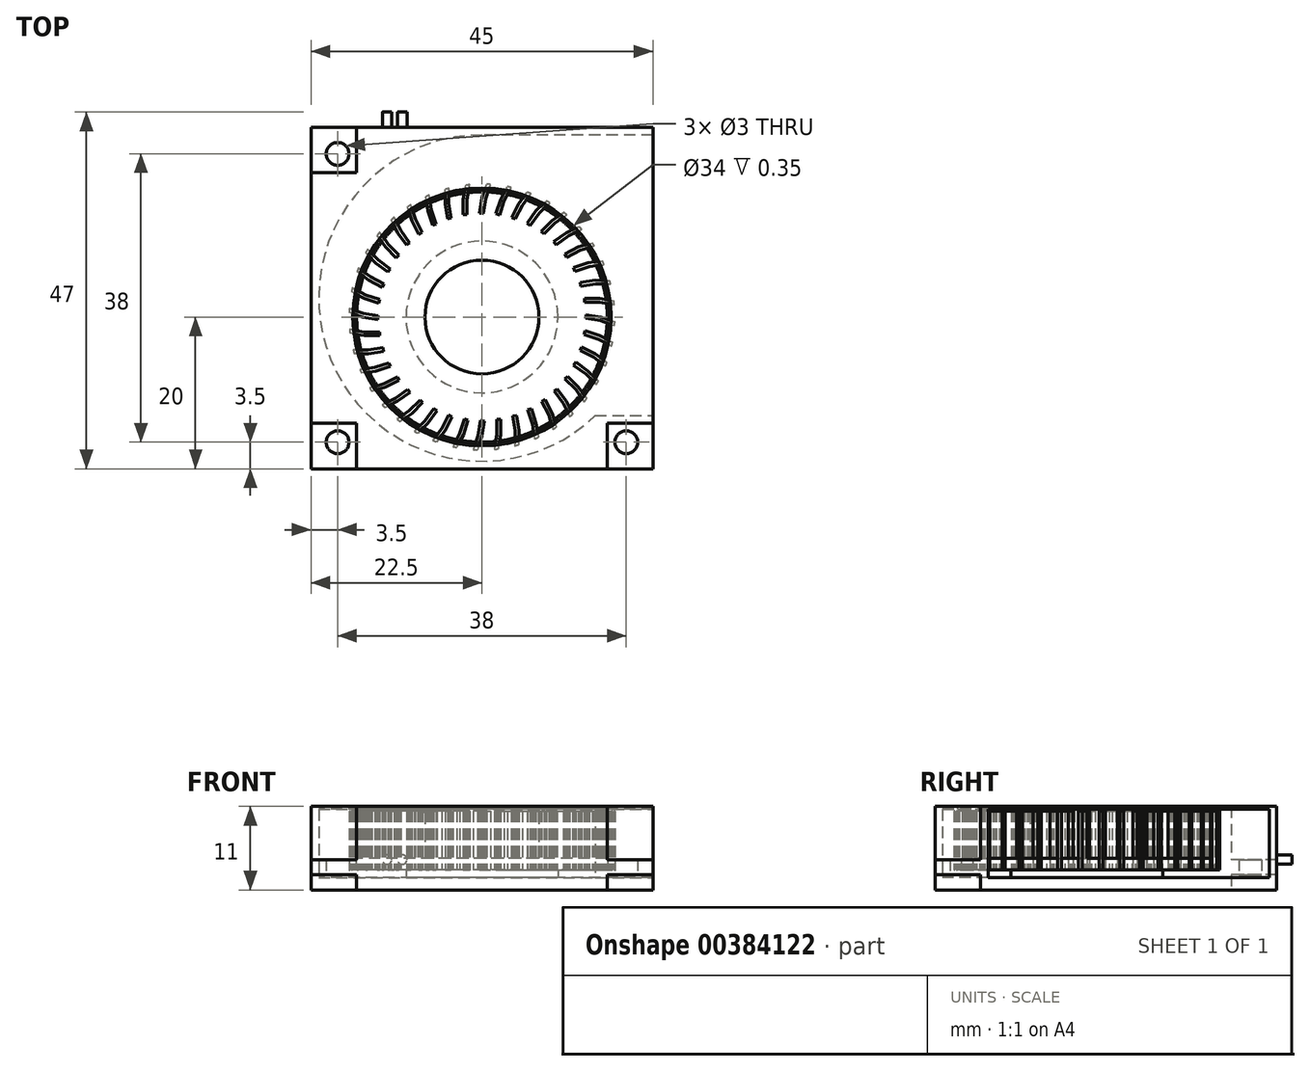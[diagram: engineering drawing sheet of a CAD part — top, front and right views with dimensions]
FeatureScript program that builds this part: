
annotation { "Feature Type Name" : "Feature", "Feature Type Description" : "" }
export const myFeature = defineFeature(function(context is Context, id is Id, definition is map)
    precondition{}
    {
        {
            var Q0;
            Q0=qCreatedBy(makeId("Top.planeOp"),FACE);
            var sketch = newSketch(context, id + "F0", { "sketchPlane" : qUnion([Q0])});
            skLineSegment(sketch, "E0", {"start": v(0, 27.21) * mm, "end": v(0, -23.79) * mm, "construction": true});
            skLineSegment(sketch, "E1", {"start": v(-25.54, 0) * mm, "end": v(25.6, 0) * mm, "construction": true});
            skLineSegment(sketch, "E2.bottom", {"start": v(-16.5, 25) * mm, "end": v(22.5, 25) * mm});
            skLineSegment(sketch, "E2.top", {"start": v(-16.5, -20) * mm, "end": v(16.5, -20) * mm});
            skLineSegment(sketch, "E2.left", {"start": v(-22.5, 19) * mm, "end": v(-22.5, -14) * mm});
            skLineSegment(sketch, "E2.right", {"start": v(22.5, 25) * mm, "end": v(22.5, -14) * mm});
            skLineSegment(sketch, "E3", {"start": v(-22.5, 19) * mm, "end": v(-16.5, 19) * mm});
            skLineSegment(sketch, "E4", {"start": v(-16.5, 19) * mm, "end": v(-16.5, 25) * mm});
            skLineSegment(sketch, "E5", {"start": v(-16.5, -14) * mm, "end": v(-16.5, -20) * mm});
            skLineSegment(sketch, "E6", {"start": v(-16.5, -14) * mm, "end": v(-22.5, -14) * mm});
            skLineSegment(sketch, "E7", {"start": v(16.5, -14) * mm, "end": v(16.5, -20) * mm});
            skLineSegment(sketch, "E8", {"start": v(16.5, -14) * mm, "end": v(22.5, -14) * mm});
            skLineSegment(sketch, "E9", {"start": v(-25.95, 2.5) * mm, "end": v(25.4, 2.5) * mm, "construction": true});
            skSolve(sketch);
        }
        {
            var Q0;
            Q0=qSketchRegion(id+"F0",true);
            extrude(context, id + "F1", {"entities" : qUnion([Q0]), "depth" : 11 * mm, "offsetDistance" : 25 * mm});
        }
        {
            var Q0;
            Q0=qCreatedBy(makeId("Top.planeOp"),FACE);
            cPlane(context, id + "F2", {"entities" : qUnion([Q0]), "cplaneType" : CPlaneType.OFFSET, "offset" : 2 * mm, "width" : 150 * mm, "height" : 150 * mm});
        }
        {
            var Q0;
            Q0=qCreatedBy(id+"F2.planeOp",FACE);
            var sketch = newSketch(context, id + "F3", { "sketchPlane" : qUnion([Q0])});
            skCircle(sketch, "E10", {"center": v(-19, 21.5) * mm, "radius": 1.5 * mm});
            skCircle(sketch, "E11", {"center": v(-19, -16.5) * mm, "radius": 1.5 * mm});
            skCircle(sketch, "E12", {"center": v(19, -16.5) * mm, "radius": 1.5 * mm});
            skLineSegment(sketch, "E13", {"start": v(-26.25, 2.5) * mm, "end": v(24.75, 2.5) * mm, "construction": true});
            skLineSegment(sketch, "E14.bottom", {"start": v(-22.5, 25) * mm, "end": v(-16.5, 25) * mm});
            skLineSegment(sketch, "E14.top", {"start": v(-22.5, 19) * mm, "end": v(-16.5, 19) * mm});
            skLineSegment(sketch, "E14.left", {"start": v(-16.5, 25) * mm, "end": v(-16.5, 19) * mm});
            skLineSegment(sketch, "E14.right", {"start": v(-22.5, 25) * mm, "end": v(-22.5, 19) * mm});
            skLineSegment(sketch, "E15.bottom", {"start": v(-22.5, -14) * mm, "end": v(-16.5, -14) * mm});
            skLineSegment(sketch, "E15.top", {"start": v(-22.5, -20) * mm, "end": v(-16.5, -20) * mm});
            skLineSegment(sketch, "E15.left", {"start": v(-16.5, -14) * mm, "end": v(-16.5, -20) * mm});
            skLineSegment(sketch, "E15.right", {"start": v(-22.5, -14) * mm, "end": v(-22.5, -20) * mm});
            skLineSegment(sketch, "E16.bottom", {"start": v(16.5, -14) * mm, "end": v(22.5, -14) * mm});
            skLineSegment(sketch, "E16.top", {"start": v(16.5, -20) * mm, "end": v(22.5, -20) * mm});
            skLineSegment(sketch, "E16.left", {"start": v(22.5, -14) * mm, "end": v(22.5, -20) * mm});
            skLineSegment(sketch, "E16.right", {"start": v(16.5, -14) * mm, "end": v(16.5, -20) * mm});
            skSolve(sketch);
        }
        {
            var Q0;
            Q0=qSketchRegion(id+"F3",true);
            extrude(context, id + "F4", {"entities" : qUnion([Q0]), "operationType" : NewBodyOperationType.ADD, "depth" : 2 * mm, "offsetDistance" : 25 * mm});
        }
        {
            var Q0;
            Q0=qCreatedBy(makeId("Top.planeOp"),FACE);
            cPlane(context, id + "F5", {"entities" : qUnion([Q0]), "cplaneType" : CPlaneType.OFFSET, "offset" : 1.65 * mm, "width" : 150 * mm, "height" : 150 * mm});
        }
        {
            var Q0;
            Q0=qCreatedBy(id+"F5.planeOp",FACE);
            var sketch = newSketch(context, id + "F6", { "sketchPlane" : qUnion([Q0])});
            skLineSegment(sketch, "E17", {"start": v(22.5, 24) * mm, "end": v(0, 24) * mm});
            skArc(sketch, "E18", {"start": v(0, 24) * mm, "mid": v(-19.94, -5.53) * mm, "end": v(14.9, -13) * mm});
            skLineSegment(sketch, "E19", {"start": v(14.9, -13) * mm, "end": v(22.5, -13) * mm});
            skLineSegment(sketch, "E20", {"start": v(22.5, -13) * mm, "end": v(22.5, 24) * mm});
            skSolve(sketch);
        }
        {
            var Q0;
            Q0=qSketchRegion(id+"F6",true);
            extrude(context, id + "F7", {"entities" : qUnion([Q0]), "operationType" : NewBodyOperationType.REMOVE, "depth" : 9 * mm, "offsetDistance" : 25 * mm});
        }
        {
            var Q0;
            Q0=makeQuery(id+"F1.opExtrude","CAP_FACE",FACE,{"disambiguationData":[OSD([sQuery(id+"F0.wireOp",EDGE,"E2.bottom"),sQuery(id+"F0.wireOp",EDGE,"E2.top"),sQuery(id+"F0.wireOp",EDGE,"E2.left"),sQuery(id+"F0.wireOp",EDGE,"E2.right"),sQuery(id+"F0.wireOp",EDGE,"E3"),sQuery(id+"F0.wireOp",EDGE,"E4"),sQuery(id+"F0.wireOp",EDGE,"E5"),sQuery(id+"F0.wireOp",EDGE,"E6"),sQuery(id+"F0.wireOp",EDGE,"E7"),sQuery(id+"F0.wireOp",EDGE,"E8")])],"isStart":false});
            var sketch = newSketch(context, id + "F8", { "sketchPlane" : qUnion([Q0])});
            skCircle(sketch, "E21", {"center": v(0, 0) * mm, "radius": 17 * mm});
            skSolve(sketch);
        }
        {
            var Q0;
            Q0=qSketchRegion(id+"F8",true);
            var Q1;
            Q1=makeQuery(id+"F7.boolean.opBoolean","COPY",FACE,{"derivedFrom":makeQuery(id+"F7.opExtrude","CAP_FACE",FACE,{"disambiguationData":[OSD([sQuery(id+"F6.wireOp",EDGE,"E17"),sQuery(id+"F6.wireOp",EDGE,"E18"),sQuery(id+"F6.wireOp",EDGE,"E19"),sQuery(id+"F6.wireOp",EDGE,"E20")])],"isStart":false})});
            extrude(context, id + "F9", {"entities" : qUnion([Q0]), "operationType" : NewBodyOperationType.REMOVE, "endBound" : BoundingType.UP_TO_SURFACE, "oppositeDirection" : true, "depth" : 25 * mm, "endBoundEntityFace" : qUnion([Q1]), "offsetDistance" : 25 * mm});
        }
        {
            var Q0;
            Q0=makeQuery(id+"F7.boolean.opBoolean","COPY",FACE,{"derivedFrom":makeQuery(id+"F7.opExtrude","CAP_FACE",FACE,{"disambiguationData":[OSD([sQuery(id+"F6.wireOp",EDGE,"E17"),sQuery(id+"F6.wireOp",EDGE,"E18"),sQuery(id+"F6.wireOp",EDGE,"E19"),sQuery(id+"F6.wireOp",EDGE,"E20")])],"isStart":true})});
            var sketch = newSketch(context, id + "F10", { "sketchPlane" : qUnion([Q0])});
            skCircle(sketch, "E22", {"center": v(0, 0) * mm, "radius": 10 * mm});
            skSolve(sketch);
        }
        {
            var Q0;
            Q0=qSketchRegion(id+"F10",true);
            extrude(context, id + "F11", {"entities" : qUnion([Q0]), "operationType" : NewBodyOperationType.ADD, "depth" : 1 * mm, "offsetDistance" : 25 * mm});
        }
        {
            var Q0;
            Q0=makeQuery(id+"F11.opExtrude","CAP_FACE",FACE,{"disambiguationData":[OSD([sQuery(id+"F10.wireOp",EDGE,"E22")])],"isStart":false});
            var sketch = newSketch(context, id + "F12", { "sketchPlane" : qUnion([Q0])});
            skCircle(sketch, "E23", {"center": v(0, 0) * mm, "radius": 17.5 * mm});
            skSolve(sketch);
        }
        {
            var Q0;
            Q0=qSketchRegion(id+"F12",true);
            extrude(context, id + "F13", {"entities" : qUnion([Q0]), "depth" : 1.5 * mm, "offsetDistance" : 25 * mm});
        }
        {
            var Q0;
            Q0=makeQuery(id+"F13.opExtrude","CAP_FACE",FACE,{"disambiguationData":[OSD([sQuery(id+"F12.wireOp",EDGE,"E23")])],"isStart":false});
            var sketch = newSketch(context, id + "F14", { "sketchPlane" : qUnion([Q0])});
            skCircle(sketch, "E24", {"center": v(0, 0) * mm, "radius": 7.5 * mm});
            skSolve(sketch);
        }
        {
            var Q0;
            Q0=qSketchRegion(id+"F14",true);
            extrude(context, id + "F15", {"entities" : qUnion([Q0]), "operationType" : NewBodyOperationType.ADD, "depth" : 6.75 * mm, "offsetDistance" : 25 * mm});
        }
        {
            var Q0;
            Q0=makeQuery(id+"F13.opExtrude","CAP_EDGE",EDGE,{"disambiguationData":[OSD([sQuery(id+"F12.wireOp",EDGE,"E23")])],"isStart":false});
            chamfer(context, id + "F16", {"entities" : qUnion([Q0]), "chamferType" : ChamferType.TWO_OFFSETS, "width1" : 10 * mm, "oppositeDirection" : false, "width2" : 1 * mm, "tangentPropagation" : true});
        }
        {
            var Q0;
            Q0=makeQuery(id+"F15.opExtrude","CAP_EDGE",EDGE,{"disambiguationData":[OSD([sQuery(id+"F14.wireOp",EDGE,"E24")])],"isStart":false});
            fillet(context, id + "F17", {"entities" : qUnion([Q0]), "radius" : 0.75 * mm, "tangentPropagation" : true, "allowEdgeOverflow" : false});
        }
        {
            var Q0;
            Q0=makeQuery(id+"F13.opExtrude","CAP_FACE",FACE,{"disambiguationData":[OSD([sQuery(id+"F12.wireOp",EDGE,"E23")])],"isStart":true});
            var sketch = newSketch(context, id + "F18", { "sketchPlane" : qUnion([Q0])});
            skLineSegment(sketch, "E25", {"start": v(13.5, -2.46) * mm, "end": v(15.5, -2.46) * mm});
            skLineSegment(sketch, "E26", {"start": v(15.5, -2.46) * mm, "end": v(17.37, -2.13) * mm});
            skLineSegment(sketch, "E27", {"start": v(13.5, -2.46) * mm, "end": v(13.5, -1.96) * mm});
            skLineSegment(sketch, "E28", {"start": v(13.5, -1.96) * mm, "end": v(15.5, -1.96) * mm});
            skLineSegment(sketch, "E29", {"start": v(15.5, -1.96) * mm, "end": v(17.42, -1.62) * mm});
            skArc(sketch, "E30", {"start": v(17.37, -2.13) * mm, "mid": v(17.4, -1.88) * mm, "end": v(17.42, -1.62) * mm});
            skSolve(sketch);
        }
        {
            var Q0;
            Q0=qSketchRegion(id+"F18",true);
            extrude(context, id + "F19", {"entities" : qUnion([Q0]), "oppositeDirection" : true, "depth" : 7.75 * mm, "offsetDistance" : 25 * mm});
        }
        {
            var Q0;
            Q0=makeQuery(id+"F19.opExtrude","SWEPT_BODY",BODY,{"disambiguationData":[OSD([sQuery(id+"F18.wireOp",EDGE,"E25"),sQuery(id+"F18.wireOp",EDGE,"E26"),sQuery(id+"F18.wireOp",EDGE,"E27"),sQuery(id+"F18.wireOp",EDGE,"E28"),sQuery(id+"F18.wireOp",EDGE,"E29"),sQuery(id+"F18.wireOp",EDGE,"E30")])]});
            var Q1;
            Q1=makeQuery(id+"F15.opExtrude","SWEPT_FACE",FACE,{"disambiguationData":[OSD([sQuery(id+"F14.wireOp",EDGE,"E24")])]});
            circularPattern(context, id + "F20", {"entities" : qUnion([Q0]), "axis" : qUnion([Q1]), "angle" : 360 * degree, "instanceCount" : 40, "equalSpace" : true, "computeTransformsWithoutBuiltin" : true});
        }
        {
            var Q0;
            Q0=makeQuery(id+"F4.boolean.opBoolean","MERGE",FACE,{"derivedFrom":[makeQuery(id+"F1.opExtrude","SWEPT_FACE",FACE,{"disambiguationData":[OSD([sQuery(id+"F0.wireOp",EDGE,"E2.bottom")])]}),makeQuery(id+"F4.opExtrude","SWEPT_FACE",FACE,{"disambiguationData":[OSD([sQuery(id+"F3.wireOp",EDGE,"E14.bottom")])]})]});
            var sketch = newSketch(context, id + "F21", { "sketchPlane" : qUnion([Q0])});
            skCircle(sketch, "E31", {"center": v(12.5, 4) * mm, "radius": 0.63 * mm});
            skCircle(sketch, "E32", {"center": v(10.5, 4) * mm, "radius": 0.62 * mm});
            skSolve(sketch);
        }
        {
            var Q0;
            Q0=qSketchRegion(id+"F21",true);
            extrude(context, id + "F22", {"entities" : qUnion([Q0]), "operationType" : NewBodyOperationType.ADD, "depth" : 2 * mm, "offsetDistance" : 25 * mm});
        }
    });
